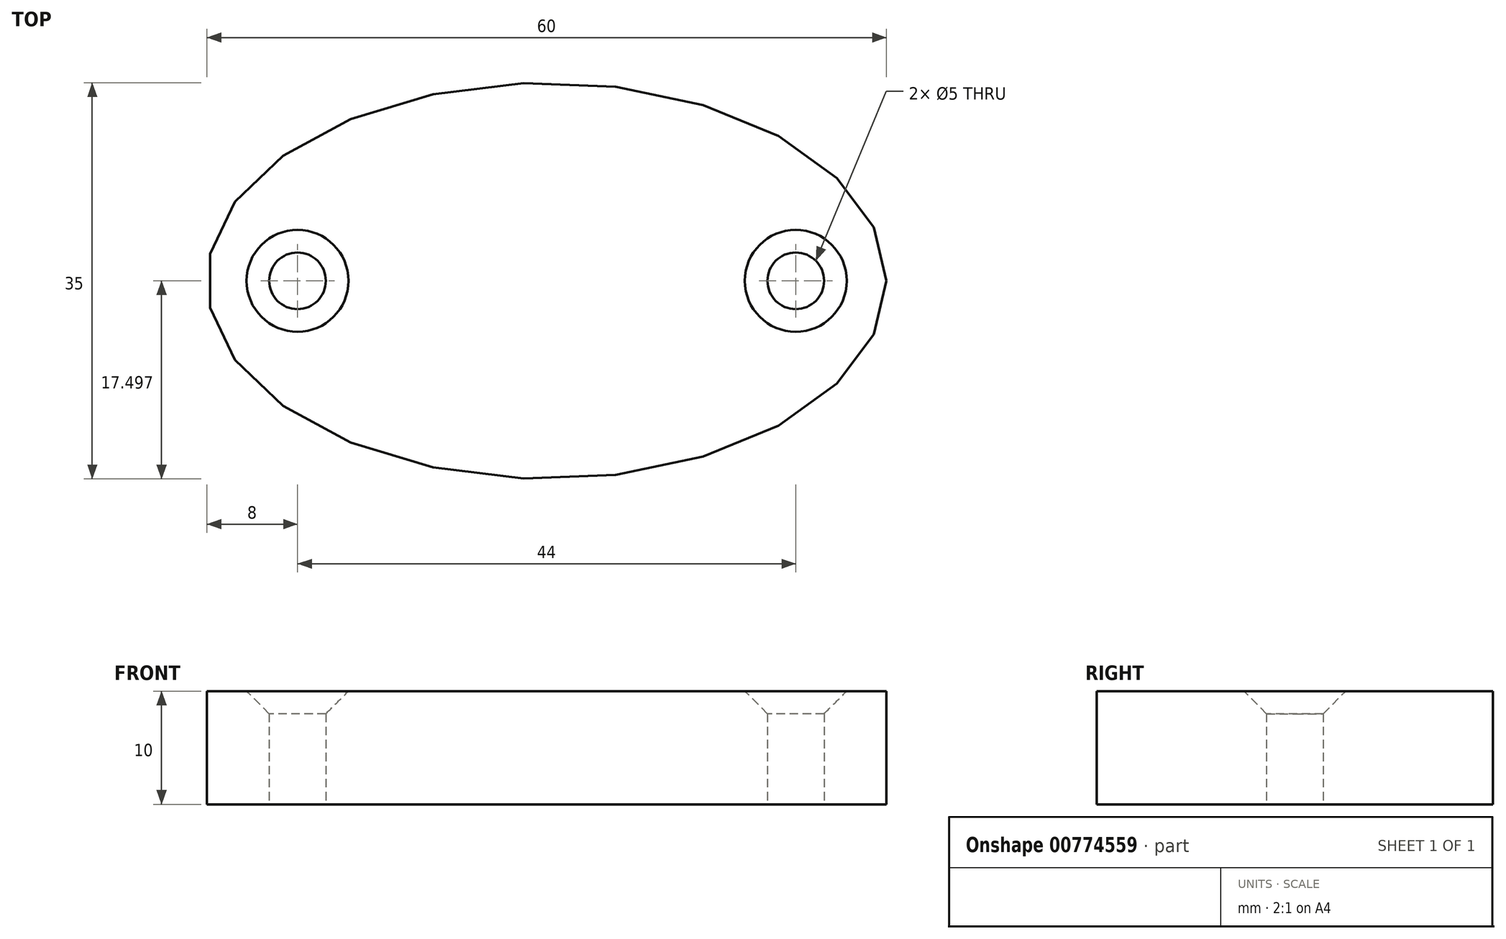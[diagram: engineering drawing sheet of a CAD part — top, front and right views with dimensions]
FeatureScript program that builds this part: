
annotation { "Feature Type Name" : "Feature", "Feature Type Description" : "" }
export const myFeature = defineFeature(function(context is Context, id is Id, definition is map)
    precondition{}
    {
        {
            var Q0;
            Q0=qCreatedBy(makeId("Top.planeOp"),FACE);
            var sketch = newSketch(context, id + "F0", { "sketchPlane" : qUnion([Q0])});
            skEllipse(sketch, "E0", {"center": v(-28.76, 24.9) * mm, "majorRadius": 17.5 * mm, "minorRadius": 30 * mm, "majorAxis": v(0, -1)});
            skCircle(sketch, "E1", {"center": v(-50.76, 24.9) * mm, "radius": 2.5 * mm});
            skPoint(sketch, "E1.centerSnap0", {"position": v(1.24, 24.9) * mm});
            skCircle(sketch, "E2", {"center": v(-6.76, 24.9) * mm, "radius": 2.5 * mm});
            skSolve(sketch);
        }
        {
            var Q0;
            Q0=makeQuery(id+"F0.imprint","IMPRINT",FACE,{"disambiguationData":[TD([[makeQuery(id+"F0.imprint","IMPRINT",EDGE,{"derivedFrom":sQuery(id+"F0.wireOp",EDGE,"E0")}),1.0]])]});
            extrude(context, id + "F1", {"entities" : qUnion([Q0]), "depth" : 10 * mm, "offsetDistance" : 25 * mm});
        }
        {
            var Q0;
            Q0=makeQuery(id+"F1.opExtrude","CAP_EDGE",EDGE,{"disambiguationData":[OSD([sQuery(id+"F0.wireOp",EDGE,"E1")])],"isStart":false});
            var Q1;
            Q1=makeQuery(id+"F1.opExtrude","CAP_EDGE",EDGE,{"disambiguationData":[OSD([sQuery(id+"F0.wireOp",EDGE,"E2")])],"isStart":false});
            chamfer(context, id + "F2", {"entities" : qUnion([Q0, Q1]), "width" : 2 * mm, "tangentPropagation" : true});
        }
    });
